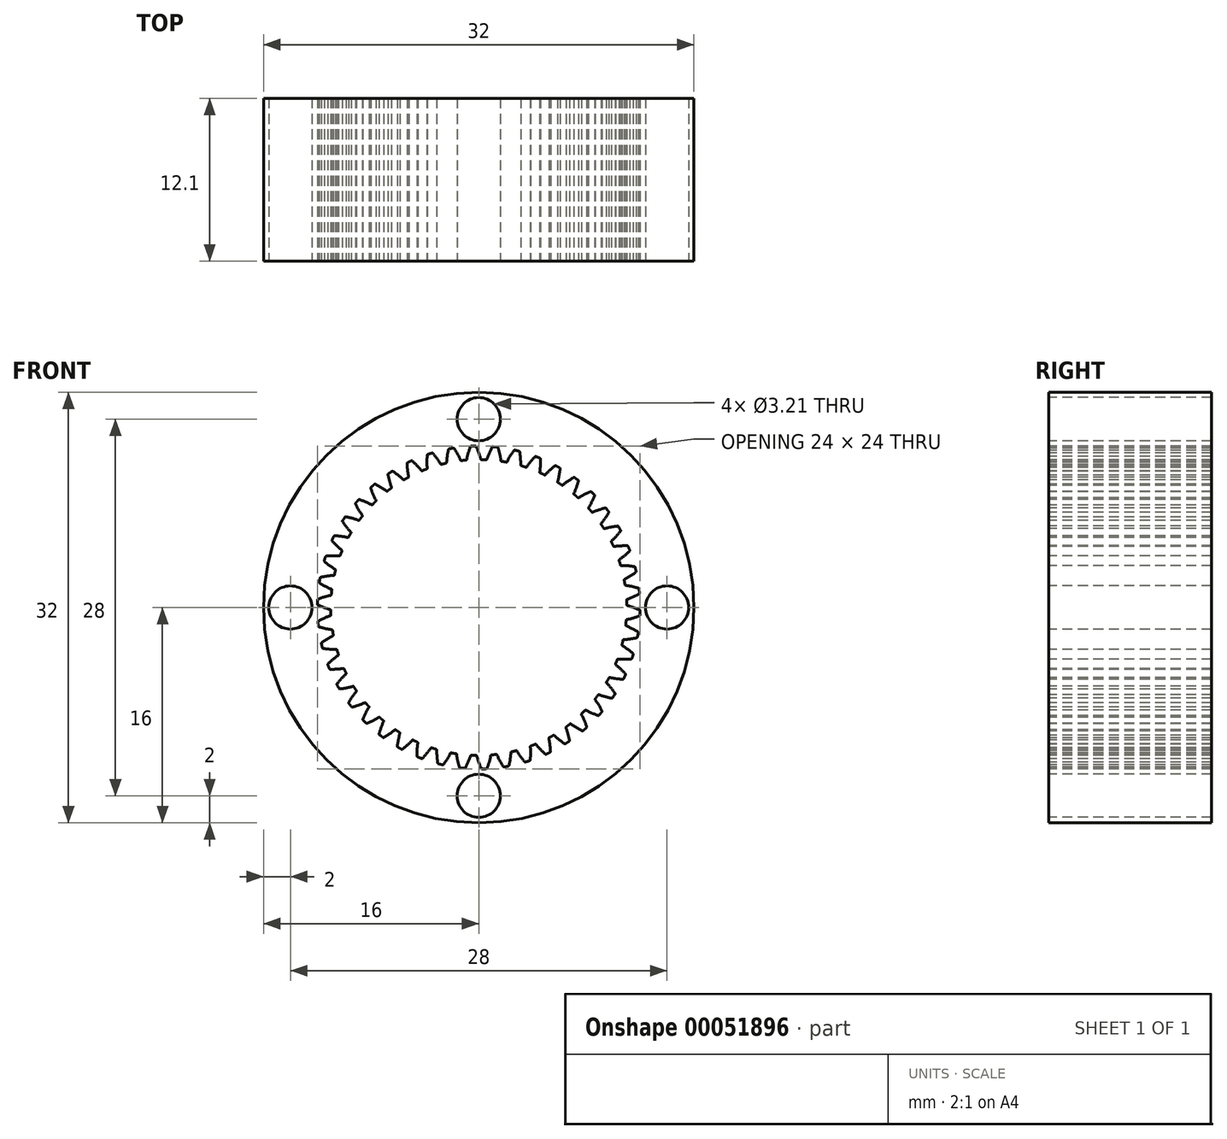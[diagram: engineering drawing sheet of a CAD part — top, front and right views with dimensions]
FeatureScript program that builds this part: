
annotation { "Feature Type Name" : "Feature", "Feature Type Description" : "" }
export const myFeature = defineFeature(function(context is Context, id is Id, definition is map)
    precondition{}
    {
        {
            var Q0;
            Q0=qCreatedBy(makeId("Front.planeOp"),FACE);
            var sketch = newSketch(context, id + "F0", { "sketchPlane" : qUnion([Q0])});
            skCircle(sketch, "E0", {"center": v(0, 0) * mm, "radius": 16 * mm});
            skSolve(sketch);
        }
        {
            var Q0;
            Q0=qSketchRegion(id+"F0",true);
            var Q1;
            Q1=makeQuery(id+"F0.imprint","IMPRINT",FACE,{"disambiguationData":[TD([[makeQuery(id+"F0.imprint","IMPRINT",EDGE,{"derivedFrom":sQuery(id+"F0.wireOp",EDGE,"E0")}),1.0]])]});
            extrude(context, id + "F1", {"entities" : qUnion([Q0, Q1]), "depth" : 12.1 * mm});
        }
        {
            var Q0;
            Q0=makeQuery(id+"F1.opExtrude","CAP_FACE",FACE,{"disambiguationData":[OSD([sQuery(id+"F0.wireOp",EDGE,"E0"),sQuery(id+"F0.wireOp",EDGE,"2902f3af-6cdb-4536-80c8-8346aa25ecb7")])],"isStart":false});
            var sketch = newSketch(context, id + "F2", { "sketchPlane" : qUnion([Q0])});
            skLineSegment(sketch, "E1", {"start": v(0, 27.51) * mm, "end": v(0, -34.9) * mm, "construction": true});
            skCircle(sketch, "E2", {"center": v(0, 14) * mm, "radius": 1.6 * mm});
            skCircle(sketch, "E3.1.0", {"center": v(-14, 0) * mm, "radius": 1.6 * mm});
            skCircle(sketch, "E3.2.0", {"center": v(0, -14) * mm, "radius": 1.6 * mm});
            skCircle(sketch, "E3.3.0", {"center": v(14, 0) * mm, "radius": 1.6 * mm});
            skPoint(sketch, "E3.center", {"position": v(0, 0) * mm});
            skSolve(sketch);
        }
        {
            var Q0;
            Q0=qSketchRegion(id+"F2",true);
            extrude(context, id + "F3", {"entities" : qUnion([Q0]), "operationType" : NewBodyOperationType.REMOVE, "endBound" : BoundingType.THROUGH_ALL, "oppositeDirection" : true, "depth" : 25 * mm});
        }
        {
            var Q0;
            Q0=makeQuery(id+"F1.opExtrude","CAP_FACE",FACE,{"disambiguationData":[OSD([sQuery(id+"F0.wireOp",EDGE,"E0")])],"isStart":false});
            var sketch = newSketch(context, id + "F4", { "sketchPlane" : qUnion([Q0])});
            skCircle(sketch, "E4", {"center": v(0, 0) * mm, "radius": 12 * mm, "construction": true});
            skCircle(sketch, "E5", {"center": v(0, 0) * mm, "radius": 11.5 * mm, "construction": true});
            skCircle(sketch, "E6", {"center": v(0, 0) * mm, "radius": 11 * mm, "construction": true});
            skLineSegment(sketch, "E7", {"start": v(0, 0) * mm, "end": v(0, 20.22) * mm, "construction": true});
            skLineSegment(sketch, "E8", {"start": v(0, 0) * mm, "end": v(-0.7, 20.22) * mm, "construction": true});
            skLineSegment(sketch, "E9", {"start": v(0, 11.5) * mm, "end": v(-8.2, 11.5) * mm, "construction": true});
            skLineSegment(sketch, "E10", {"start": v(0, 11.5) * mm, "end": v(-7.4, 8.8) * mm, "construction": true});
            skCircle(sketch, "E11", {"center": v(0, 11.5) * mm, "radius": 5.75 * mm, "construction": true});
            skCircle(sketch, "E12", {"center": v(-5.4, 9.53) * mm, "radius": 5.75 * mm, "construction": true});
            skArc(sketch, "E13", {"start": v(-0.2, 12) * mm, "mid": v(0, 11.5) * mm, "end": v(0.16, 11) * mm, "construction": true});
            skArc(sketch, "E14.MirrorCS", {"start": v(-0.61, 11.98) * mm, "mid": v(-0.78, 11.48) * mm, "end": v(-0.9, 10.96) * mm, "construction": true});
            skArc(sketch, "E15", {"start": v(-0.62, 11.95) * mm, "mid": v(-0.78, 11.48) * mm, "end": v(-0.9, 11) * mm});
            skArc(sketch, "E16", {"start": v(-0.58, 11.99) * mm, "mid": v(-0.4, 12) * mm, "end": v(-0.24, 12) * mm});
            skArc(sketch, "E17", {"start": v(-0.2, 11.97) * mm, "mid": v(0, 11.5) * mm, "end": v(0.15, 11.04) * mm});
            skArc(sketch, "E18", {"start": v(-0.94, 10.96) * mm, "mid": v(0.38, -11) * mm, "end": v(0.2, 11) * mm});
            skPoint(sketch, "E19.visualSharp", {"position": v(-0.9, 10.96) * mm});
            skArc(sketch, "E19.filletArc", {"start": v(-0.94, 10.96) * mm, "mid": v(-0.92, 10.97) * mm, "end": v(-0.9, 11) * mm});
            skPoint(sketch, "E20.visualSharp", {"position": v(-0.61, 11.98) * mm});
            skArc(sketch, "E20.filletArc", {"start": v(-0.58, 11.99) * mm, "mid": v(-0.6, 11.98) * mm, "end": v(-0.62, 11.95) * mm});
            skPoint(sketch, "E21.visualSharp", {"position": v(-0.2, 12) * mm});
            skArc(sketch, "E21.filletArc", {"start": v(-0.2, 11.97) * mm, "mid": v(-0.21, 12) * mm, "end": v(-0.24, 12) * mm});
            skPoint(sketch, "E22.visualSharp", {"position": v(0.16, 11) * mm});
            skArc(sketch, "E22.filletArc", {"start": v(0.15, 11.04) * mm, "mid": v(0.16, 11) * mm, "end": v(0.2, 11) * mm});
            skArc(sketch, "E23.1.0", {"start": v(-2.43, 10.73) * mm, "mid": v(-2.4, 10.75) * mm, "end": v(-2.39, 10.77) * mm});
            skArc(sketch, "E23.1.1", {"start": v(-2.24, 11.76) * mm, "mid": v(-2.34, 11.27) * mm, "end": v(-2.39, 10.77) * mm});
            skArc(sketch, "E23.1.2", {"start": v(-2.2, 11.8) * mm, "mid": v(-2.23, 11.78) * mm, "end": v(-2.24, 11.76) * mm});
            skArc(sketch, "E23.1.3", {"start": v(-2.2, 11.8) * mm, "mid": v(-2.04, 11.83) * mm, "end": v(-1.87, 11.85) * mm});
            skArc(sketch, "E23.1.4", {"start": v(-1.82, 11.83) * mm, "mid": v(-1.84, 11.85) * mm, "end": v(-1.87, 11.85) * mm});
            skArc(sketch, "E23.1.5", {"start": v(-1.82, 11.83) * mm, "mid": v(-1.57, 11.4) * mm, "end": v(-1.36, 10.95) * mm});
            skArc(sketch, "E23.1.6", {"start": v(-1.36, 10.95) * mm, "mid": v(-1.34, 10.93) * mm, "end": v(-1.3, 10.92) * mm});
            skArc(sketch, "E23.2.0", {"start": v(-3.87, 10.3) * mm, "mid": v(-3.84, 10.32) * mm, "end": v(-3.83, 10.35) * mm});
            skArc(sketch, "E23.2.1", {"start": v(-3.82, 11.34) * mm, "mid": v(-3.85, 10.85) * mm, "end": v(-3.83, 10.35) * mm});
            skArc(sketch, "E23.2.2", {"start": v(-3.8, 11.39) * mm, "mid": v(-3.81, 11.37) * mm, "end": v(-3.82, 11.34) * mm});
            skArc(sketch, "E23.2.3", {"start": v(-3.8, 11.39) * mm, "mid": v(-3.63, 11.44) * mm, "end": v(-3.47, 11.49) * mm});
            skArc(sketch, "E23.2.4", {"start": v(-3.42, 11.47) * mm, "mid": v(-3.44, 11.49) * mm, "end": v(-3.47, 11.49) * mm});
            skArc(sketch, "E23.2.5", {"start": v(-3.42, 11.47) * mm, "mid": v(-3.1, 11.08) * mm, "end": v(-2.84, 10.67) * mm});
            skArc(sketch, "E23.2.6", {"start": v(-2.84, 10.67) * mm, "mid": v(-2.81, 10.65) * mm, "end": v(-2.78, 10.64) * mm});
            skArc(sketch, "E23.3.0", {"start": v(-5.23, 9.68) * mm, "mid": v(-5.21, 9.7) * mm, "end": v(-5.2, 9.73) * mm});
            skArc(sketch, "E23.3.1", {"start": v(-5.33, 10.72) * mm, "mid": v(-5.3, 10.22) * mm, "end": v(-5.2, 9.73) * mm});
            skArc(sketch, "E23.3.2", {"start": v(-5.3, 10.76) * mm, "mid": v(-5.33, 10.74) * mm, "end": v(-5.33, 10.72) * mm});
            skArc(sketch, "E23.3.3", {"start": v(-5.3, 10.76) * mm, "mid": v(-5.15, 10.84) * mm, "end": v(-5, 10.9) * mm});
            skArc(sketch, "E23.3.4", {"start": v(-4.95, 10.9) * mm, "mid": v(-4.97, 10.91) * mm, "end": v(-5, 10.9) * mm});
            skArc(sketch, "E23.3.5", {"start": v(-4.95, 10.9) * mm, "mid": v(-4.59, 10.56) * mm, "end": v(-4.26, 10.18) * mm});
            skArc(sketch, "E23.3.6", {"start": v(-4.26, 10.18) * mm, "mid": v(-4.23, 10.16) * mm, "end": v(-4.2, 10.17) * mm});
            skArc(sketch, "E23.4.0", {"start": v(-6.5, 8.87) * mm, "mid": v(-6.48, 8.9) * mm, "end": v(-6.48, 8.93) * mm});
            skArc(sketch, "E23.4.1", {"start": v(-6.74, 9.9) * mm, "mid": v(-6.63, 9.4) * mm, "end": v(-6.48, 8.93) * mm});
            skArc(sketch, "E23.4.2", {"start": v(-6.72, 9.94) * mm, "mid": v(-6.74, 9.92) * mm, "end": v(-6.74, 9.9) * mm});
            skArc(sketch, "E23.4.3", {"start": v(-6.72, 9.94) * mm, "mid": v(-6.58, 10.03) * mm, "end": v(-6.44, 10.13) * mm});
            skArc(sketch, "E23.4.4", {"start": v(-6.38, 10.13) * mm, "mid": v(-6.41, 10.13) * mm, "end": v(-6.44, 10.13) * mm});
            skArc(sketch, "E23.4.5", {"start": v(-6.38, 10.13) * mm, "mid": v(-5.98, 9.83) * mm, "end": v(-5.6, 9.5) * mm});
            skArc(sketch, "E23.4.6", {"start": v(-5.6, 9.5) * mm, "mid": v(-5.58, 9.5) * mm, "end": v(-5.55, 9.5) * mm});
            skArc(sketch, "E23.5.0", {"start": v(-7.65, 7.9) * mm, "mid": v(-7.63, 7.93) * mm, "end": v(-7.64, 7.96) * mm});
            skArc(sketch, "E23.5.1", {"start": v(-8.03, 8.88) * mm, "mid": v(-7.85, 8.41) * mm, "end": v(-7.64, 7.96) * mm});
            skArc(sketch, "E23.5.2", {"start": v(-8.01, 8.93) * mm, "mid": v(-8.03, 8.9) * mm, "end": v(-8.03, 8.88) * mm});
            skArc(sketch, "E23.5.3", {"start": v(-8.01, 8.93) * mm, "mid": v(-7.89, 9.04) * mm, "end": v(-7.76, 9.15) * mm});
            skArc(sketch, "E23.5.4", {"start": v(-7.7, 9.16) * mm, "mid": v(-7.73, 9.17) * mm, "end": v(-7.76, 9.15) * mm});
            skArc(sketch, "E23.5.5", {"start": v(-7.7, 9.16) * mm, "mid": v(-7.27, 8.93) * mm, "end": v(-6.85, 8.65) * mm});
            skArc(sketch, "E23.5.6", {"start": v(-6.85, 8.65) * mm, "mid": v(-6.82, 8.64) * mm, "end": v(-6.79, 8.65) * mm});
            skArc(sketch, "E23.6.0", {"start": v(-8.65, 6.79) * mm, "mid": v(-8.64, 6.82) * mm, "end": v(-8.65, 6.85) * mm});
            skArc(sketch, "E23.6.1", {"start": v(-9.16, 7.7) * mm, "mid": v(-8.93, 7.27) * mm, "end": v(-8.65, 6.85) * mm});
            skArc(sketch, "E23.6.2", {"start": v(-9.15, 7.76) * mm, "mid": v(-9.17, 7.73) * mm, "end": v(-9.16, 7.7) * mm});
            skArc(sketch, "E23.6.3", {"start": v(-9.15, 7.76) * mm, "mid": v(-9.04, 7.89) * mm, "end": v(-8.93, 8.01) * mm});
            skArc(sketch, "E23.6.4", {"start": v(-8.88, 8.03) * mm, "mid": v(-8.9, 8.03) * mm, "end": v(-8.93, 8.01) * mm});
            skArc(sketch, "E23.6.5", {"start": v(-8.88, 8.03) * mm, "mid": v(-8.41, 7.85) * mm, "end": v(-7.96, 7.64) * mm});
            skArc(sketch, "E23.6.6", {"start": v(-7.96, 7.64) * mm, "mid": v(-7.93, 7.63) * mm, "end": v(-7.9, 7.65) * mm});
            skArc(sketch, "E23.7.0", {"start": v(-9.5, 5.55) * mm, "mid": v(-9.5, 5.58) * mm, "end": v(-9.5, 5.6) * mm});
            skArc(sketch, "E23.7.1", {"start": v(-10.13, 6.38) * mm, "mid": v(-9.83, 5.98) * mm, "end": v(-9.5, 5.6) * mm});
            skArc(sketch, "E23.7.2", {"start": v(-10.13, 6.44) * mm, "mid": v(-10.13, 6.41) * mm, "end": v(-10.13, 6.38) * mm});
            skArc(sketch, "E23.7.3", {"start": v(-10.13, 6.44) * mm, "mid": v(-10.03, 6.58) * mm, "end": v(-9.94, 6.72) * mm});
            skArc(sketch, "E23.7.4", {"start": v(-9.9, 6.74) * mm, "mid": v(-9.92, 6.74) * mm, "end": v(-9.94, 6.72) * mm});
            skArc(sketch, "E23.7.5", {"start": v(-9.9, 6.74) * mm, "mid": v(-9.4, 6.63) * mm, "end": v(-8.93, 6.48) * mm});
            skArc(sketch, "E23.7.6", {"start": v(-8.93, 6.48) * mm, "mid": v(-8.9, 6.48) * mm, "end": v(-8.87, 6.5) * mm});
            skArc(sketch, "E23.8.0", {"start": v(-10.17, 4.2) * mm, "mid": v(-10.16, 4.23) * mm, "end": v(-10.18, 4.26) * mm});
            skArc(sketch, "E23.8.1", {"start": v(-10.9, 4.95) * mm, "mid": v(-10.56, 4.59) * mm, "end": v(-10.18, 4.26) * mm});
            skArc(sketch, "E23.8.2", {"start": v(-10.9, 5) * mm, "mid": v(-10.91, 4.97) * mm, "end": v(-10.9, 4.95) * mm});
            skArc(sketch, "E23.8.3", {"start": v(-10.9, 5) * mm, "mid": v(-10.84, 5.15) * mm, "end": v(-10.76, 5.3) * mm});
            skArc(sketch, "E23.8.4", {"start": v(-10.72, 5.33) * mm, "mid": v(-10.74, 5.33) * mm, "end": v(-10.76, 5.3) * mm});
            skArc(sketch, "E23.8.5", {"start": v(-10.72, 5.33) * mm, "mid": v(-10.22, 5.3) * mm, "end": v(-9.73, 5.2) * mm});
            skArc(sketch, "E23.8.6", {"start": v(-9.73, 5.2) * mm, "mid": v(-9.7, 5.21) * mm, "end": v(-9.68, 5.23) * mm});
            skArc(sketch, "E23.9.0", {"start": v(-10.64, 2.78) * mm, "mid": v(-10.65, 2.81) * mm, "end": v(-10.67, 2.84) * mm});
            skArc(sketch, "E23.9.1", {"start": v(-11.47, 3.42) * mm, "mid": v(-11.08, 3.1) * mm, "end": v(-10.67, 2.84) * mm});
            skArc(sketch, "E23.9.2", {"start": v(-11.49, 3.47) * mm, "mid": v(-11.49, 3.44) * mm, "end": v(-11.47, 3.42) * mm});
            skArc(sketch, "E23.9.3", {"start": v(-11.49, 3.47) * mm, "mid": v(-11.44, 3.63) * mm, "end": v(-11.39, 3.8) * mm});
            skArc(sketch, "E23.9.4", {"start": v(-11.34, 3.82) * mm, "mid": v(-11.37, 3.81) * mm, "end": v(-11.39, 3.8) * mm});
            skArc(sketch, "E23.9.5", {"start": v(-11.34, 3.82) * mm, "mid": v(-10.85, 3.85) * mm, "end": v(-10.35, 3.83) * mm});
            skArc(sketch, "E23.9.6", {"start": v(-10.35, 3.83) * mm, "mid": v(-10.32, 3.84) * mm, "end": v(-10.3, 3.87) * mm});
            skArc(sketch, "E23.10.0", {"start": v(-10.92, 1.3) * mm, "mid": v(-10.93, 1.34) * mm, "end": v(-10.95, 1.36) * mm});
            skArc(sketch, "E23.10.1", {"start": v(-11.83, 1.82) * mm, "mid": v(-11.4, 1.57) * mm, "end": v(-10.95, 1.36) * mm});
            skArc(sketch, "E23.10.2", {"start": v(-11.85, 1.87) * mm, "mid": v(-11.85, 1.84) * mm, "end": v(-11.83, 1.82) * mm});
            skArc(sketch, "E23.10.3", {"start": v(-11.85, 1.87) * mm, "mid": v(-11.83, 2.04) * mm, "end": v(-11.8, 2.2) * mm});
            skArc(sketch, "E23.10.4", {"start": v(-11.76, 2.24) * mm, "mid": v(-11.78, 2.23) * mm, "end": v(-11.8, 2.2) * mm});
            skArc(sketch, "E23.10.5", {"start": v(-11.76, 2.24) * mm, "mid": v(-11.27, 2.34) * mm, "end": v(-10.77, 2.39) * mm});
            skArc(sketch, "E23.10.6", {"start": v(-10.77, 2.39) * mm, "mid": v(-10.75, 2.4) * mm, "end": v(-10.73, 2.43) * mm});
            skArc(sketch, "E23.11.0", {"start": v(-11, -0.2) * mm, "mid": v(-11, -0.16) * mm, "end": v(-11.04, -0.15) * mm});
            skArc(sketch, "E23.11.1", {"start": v(-11.97, 0.2) * mm, "mid": v(-11.5, 0) * mm, "end": v(-11.04, -0.15) * mm});
            skArc(sketch, "E23.11.2", {"start": v(-12, 0.24) * mm, "mid": v(-12, 0.21) * mm, "end": v(-11.97, 0.2) * mm});
            skArc(sketch, "E23.11.3", {"start": v(-12, 0.24) * mm, "mid": v(-12, 0.4) * mm, "end": v(-11.99, 0.58) * mm});
            skArc(sketch, "E23.11.4", {"start": v(-11.95, 0.62) * mm, "mid": v(-11.98, 0.6) * mm, "end": v(-11.99, 0.58) * mm});
            skArc(sketch, "E23.11.5", {"start": v(-11.95, 0.62) * mm, "mid": v(-11.48, 0.78) * mm, "end": v(-11, 0.9) * mm});
            skArc(sketch, "E23.11.6", {"start": v(-11, 0.9) * mm, "mid": v(-10.97, 0.92) * mm, "end": v(-10.96, 0.94) * mm});
            skArc(sketch, "E23.12.0", {"start": v(-10.87, -1.7) * mm, "mid": v(-10.88, -1.66) * mm, "end": v(-10.91, -1.65) * mm});
            skArc(sketch, "E23.12.1", {"start": v(-11.88, -1.44) * mm, "mid": v(-11.4, -1.56) * mm, "end": v(-10.91, -1.65) * mm});
            skArc(sketch, "E23.12.2", {"start": v(-11.92, -1.4) * mm, "mid": v(-11.9, -1.42) * mm, "end": v(-11.88, -1.44) * mm});
            skArc(sketch, "E23.12.3", {"start": v(-11.92, -1.4) * mm, "mid": v(-11.94, -1.23) * mm, "end": v(-11.95, -1.06) * mm});
            skArc(sketch, "E23.12.4", {"start": v(-11.93, -1.01) * mm, "mid": v(-11.95, -1.03) * mm, "end": v(-11.95, -1.06) * mm});
            skArc(sketch, "E23.12.5", {"start": v(-11.93, -1.01) * mm, "mid": v(-11.48, -0.79) * mm, "end": v(-11.02, -0.6) * mm});
            skArc(sketch, "E23.12.6", {"start": v(-11.02, -0.6) * mm, "mid": v(-11, -0.59) * mm, "end": v(-10.99, -0.56) * mm});
            skArc(sketch, "E23.13.0", {"start": v(-10.54, -3.15) * mm, "mid": v(-10.56, -3.13) * mm, "end": v(-10.59, -3.12) * mm});
            skArc(sketch, "E23.13.1", {"start": v(-11.58, -3.04) * mm, "mid": v(-11.08, -3.1) * mm, "end": v(-10.59, -3.12) * mm});
            skArc(sketch, "E23.13.2", {"start": v(-11.62, -3) * mm, "mid": v(-11.6, -3.03) * mm, "end": v(-11.58, -3.04) * mm});
            skArc(sketch, "E23.13.3", {"start": v(-11.62, -3) * mm, "mid": v(-11.66, -2.84) * mm, "end": v(-11.7, -2.68) * mm});
            skArc(sketch, "E23.13.4", {"start": v(-11.68, -2.63) * mm, "mid": v(-11.7, -2.65) * mm, "end": v(-11.7, -2.68) * mm});
            skArc(sketch, "E23.13.5", {"start": v(-11.68, -2.63) * mm, "mid": v(-11.27, -2.35) * mm, "end": v(-10.83, -2.1) * mm});
            skArc(sketch, "E23.13.6", {"start": v(-10.83, -2.1) * mm, "mid": v(-10.81, -2.08) * mm, "end": v(-10.8, -2.05) * mm});
            skArc(sketch, "E23.14.0", {"start": v(-10.01, -4.56) * mm, "mid": v(-10.03, -4.54) * mm, "end": v(-10.06, -4.53) * mm});
            skArc(sketch, "E23.14.1", {"start": v(-11.06, -4.6) * mm, "mid": v(-10.56, -4.58) * mm, "end": v(-10.06, -4.53) * mm});
            skArc(sketch, "E23.14.2", {"start": v(-11.1, -4.56) * mm, "mid": v(-11.08, -4.58) * mm, "end": v(-11.06, -4.6) * mm});
            skArc(sketch, "E23.14.3", {"start": v(-11.1, -4.56) * mm, "mid": v(-11.16, -4.4) * mm, "end": v(-11.22, -4.24) * mm});
            skArc(sketch, "E23.14.4", {"start": v(-11.21, -4.2) * mm, "mid": v(-11.23, -4.22) * mm, "end": v(-11.22, -4.24) * mm});
            skArc(sketch, "E23.14.5", {"start": v(-11.21, -4.2) * mm, "mid": v(-10.84, -3.86) * mm, "end": v(-10.45, -3.56) * mm});
            skArc(sketch, "E23.14.6", {"start": v(-10.45, -3.56) * mm, "mid": v(-10.43, -3.53) * mm, "end": v(-10.43, -3.5) * mm});
            skArc(sketch, "E23.15.0", {"start": v(-9.3, -5.88) * mm, "mid": v(-9.32, -5.86) * mm, "end": v(-9.35, -5.86) * mm});
            skArc(sketch, "E23.15.1", {"start": v(-10.33, -6.05) * mm, "mid": v(-9.84, -5.98) * mm, "end": v(-9.35, -5.86) * mm});
            skArc(sketch, "E23.15.2", {"start": v(-10.38, -6.03) * mm, "mid": v(-10.36, -6.05) * mm, "end": v(-10.33, -6.05) * mm});
            skArc(sketch, "E23.15.3", {"start": v(-10.38, -6.03) * mm, "mid": v(-10.46, -5.88) * mm, "end": v(-10.54, -5.73) * mm});
            skArc(sketch, "E23.15.4", {"start": v(-10.54, -5.68) * mm, "mid": v(-10.55, -5.7) * mm, "end": v(-10.54, -5.73) * mm});
            skArc(sketch, "E23.15.5", {"start": v(-10.54, -5.68) * mm, "mid": v(-10.22, -5.3) * mm, "end": v(-9.87, -4.95) * mm});
            skArc(sketch, "E23.15.6", {"start": v(-9.87, -4.95) * mm, "mid": v(-9.85, -4.92) * mm, "end": v(-9.85, -4.89) * mm});
            skArc(sketch, "E23.16.0", {"start": v(-8.4, -7.1) * mm, "mid": v(-8.44, -7.08) * mm, "end": v(-8.47, -7.08) * mm});
            skArc(sketch, "E23.16.1", {"start": v(-9.4, -7.4) * mm, "mid": v(-8.93, -7.26) * mm, "end": v(-8.47, -7.08) * mm});
            skArc(sketch, "E23.16.2", {"start": v(-9.46, -7.38) * mm, "mid": v(-9.44, -7.4) * mm, "end": v(-9.4, -7.4) * mm});
            skArc(sketch, "E23.16.3", {"start": v(-9.46, -7.38) * mm, "mid": v(-9.56, -7.25) * mm, "end": v(-9.66, -7.12) * mm});
            skArc(sketch, "E23.16.4", {"start": v(-9.67, -7.06) * mm, "mid": v(-9.67, -7.09) * mm, "end": v(-9.66, -7.12) * mm});
            skArc(sketch, "E23.16.5", {"start": v(-9.67, -7.06) * mm, "mid": v(-9.4, -6.64) * mm, "end": v(-9.1, -6.24) * mm});
            skArc(sketch, "E23.16.6", {"start": v(-9.1, -6.24) * mm, "mid": v(-9.09, -6.21) * mm, "end": v(-9.1, -6.18) * mm});
            skArc(sketch, "E23.17.0", {"start": v(-7.36, -8.17) * mm, "mid": v(-7.4, -8.16) * mm, "end": v(-7.42, -8.17) * mm});
            skArc(sketch, "E23.17.1", {"start": v(-8.31, -8.61) * mm, "mid": v(-7.86, -8.4) * mm, "end": v(-7.42, -8.17) * mm});
            skArc(sketch, "E23.17.2", {"start": v(-8.36, -8.6) * mm, "mid": v(-8.34, -8.62) * mm, "end": v(-8.31, -8.61) * mm});
            skArc(sketch, "E23.17.3", {"start": v(-8.36, -8.6) * mm, "mid": v(-8.49, -8.49) * mm, "end": v(-8.6, -8.36) * mm});
            skArc(sketch, "E23.17.4", {"start": v(-8.61, -8.31) * mm, "mid": v(-8.62, -8.34) * mm, "end": v(-8.6, -8.36) * mm});
            skArc(sketch, "E23.17.5", {"start": v(-8.61, -8.31) * mm, "mid": v(-8.4, -7.86) * mm, "end": v(-8.17, -7.42) * mm});
            skArc(sketch, "E23.17.6", {"start": v(-8.17, -7.42) * mm, "mid": v(-8.16, -7.4) * mm, "end": v(-8.17, -7.36) * mm});
            skArc(sketch, "E23.18.0", {"start": v(-6.18, -9.1) * mm, "mid": v(-6.21, -9.09) * mm, "end": v(-6.24, -9.1) * mm});
            skArc(sketch, "E23.18.1", {"start": v(-7.06, -9.67) * mm, "mid": v(-6.64, -9.4) * mm, "end": v(-6.24, -9.1) * mm});
            skArc(sketch, "E23.18.2", {"start": v(-7.12, -9.66) * mm, "mid": v(-7.09, -9.67) * mm, "end": v(-7.06, -9.67) * mm});
            skArc(sketch, "E23.18.3", {"start": v(-7.12, -9.66) * mm, "mid": v(-7.25, -9.56) * mm, "end": v(-7.38, -9.46) * mm});
            skArc(sketch, "E23.18.4", {"start": v(-7.4, -9.4) * mm, "mid": v(-7.4, -9.44) * mm, "end": v(-7.38, -9.46) * mm});
            skArc(sketch, "E23.18.5", {"start": v(-7.4, -9.4) * mm, "mid": v(-7.26, -8.93) * mm, "end": v(-7.08, -8.47) * mm});
            skArc(sketch, "E23.18.6", {"start": v(-7.08, -8.47) * mm, "mid": v(-7.08, -8.44) * mm, "end": v(-7.1, -8.4) * mm});
            skArc(sketch, "E23.19.0", {"start": v(-4.89, -9.85) * mm, "mid": v(-4.92, -9.85) * mm, "end": v(-4.95, -9.87) * mm});
            skArc(sketch, "E23.19.1", {"start": v(-5.68, -10.54) * mm, "mid": v(-5.3, -10.22) * mm, "end": v(-4.95, -9.87) * mm});
            skArc(sketch, "E23.19.2", {"start": v(-5.73, -10.54) * mm, "mid": v(-5.7, -10.55) * mm, "end": v(-5.68, -10.54) * mm});
            skArc(sketch, "E23.19.3", {"start": v(-5.73, -10.54) * mm, "mid": v(-5.88, -10.46) * mm, "end": v(-6.03, -10.38) * mm});
            skArc(sketch, "E23.19.4", {"start": v(-6.05, -10.33) * mm, "mid": v(-6.05, -10.36) * mm, "end": v(-6.03, -10.38) * mm});
            skArc(sketch, "E23.19.5", {"start": v(-6.05, -10.33) * mm, "mid": v(-5.98, -9.84) * mm, "end": v(-5.86, -9.35) * mm});
            skArc(sketch, "E23.19.6", {"start": v(-5.86, -9.35) * mm, "mid": v(-5.86, -9.32) * mm, "end": v(-5.88, -9.3) * mm});
            skArc(sketch, "E23.20.0", {"start": v(-3.5, -10.43) * mm, "mid": v(-3.53, -10.43) * mm, "end": v(-3.56, -10.45) * mm});
            skArc(sketch, "E23.20.1", {"start": v(-4.2, -11.21) * mm, "mid": v(-3.86, -10.84) * mm, "end": v(-3.56, -10.45) * mm});
            skArc(sketch, "E23.20.2", {"start": v(-4.24, -11.22) * mm, "mid": v(-4.22, -11.23) * mm, "end": v(-4.2, -11.21) * mm});
            skArc(sketch, "E23.20.3", {"start": v(-4.24, -11.22) * mm, "mid": v(-4.4, -11.16) * mm, "end": v(-4.56, -11.1) * mm});
            skArc(sketch, "E23.20.4", {"start": v(-4.6, -11.06) * mm, "mid": v(-4.58, -11.08) * mm, "end": v(-4.56, -11.1) * mm});
            skArc(sketch, "E23.20.5", {"start": v(-4.6, -11.06) * mm, "mid": v(-4.58, -10.56) * mm, "end": v(-4.53, -10.06) * mm});
            skArc(sketch, "E23.20.6", {"start": v(-4.53, -10.06) * mm, "mid": v(-4.54, -10.03) * mm, "end": v(-4.56, -10.01) * mm});
            skArc(sketch, "E23.21.0", {"start": v(-2.05, -10.8) * mm, "mid": v(-2.08, -10.81) * mm, "end": v(-2.1, -10.83) * mm});
            skArc(sketch, "E23.21.1", {"start": v(-2.63, -11.68) * mm, "mid": v(-2.35, -11.27) * mm, "end": v(-2.1, -10.83) * mm});
            skArc(sketch, "E23.21.2", {"start": v(-2.68, -11.7) * mm, "mid": v(-2.65, -11.7) * mm, "end": v(-2.63, -11.68) * mm});
            skArc(sketch, "E23.21.3", {"start": v(-2.68, -11.7) * mm, "mid": v(-2.84, -11.66) * mm, "end": v(-3, -11.62) * mm});
            skArc(sketch, "E23.21.4", {"start": v(-3.04, -11.58) * mm, "mid": v(-3.03, -11.6) * mm, "end": v(-3, -11.62) * mm});
            skArc(sketch, "E23.21.5", {"start": v(-3.04, -11.58) * mm, "mid": v(-3.1, -11.08) * mm, "end": v(-3.12, -10.59) * mm});
            skArc(sketch, "E23.21.6", {"start": v(-3.12, -10.59) * mm, "mid": v(-3.13, -10.56) * mm, "end": v(-3.15, -10.54) * mm});
            skArc(sketch, "E23.22.0", {"start": v(-0.56, -10.99) * mm, "mid": v(-0.59, -11) * mm, "end": v(-0.6, -11.02) * mm});
            skArc(sketch, "E23.22.1", {"start": v(-1.01, -11.93) * mm, "mid": v(-0.79, -11.48) * mm, "end": v(-0.6, -11.02) * mm});
            skArc(sketch, "E23.22.2", {"start": v(-1.06, -11.95) * mm, "mid": v(-1.03, -11.95) * mm, "end": v(-1.01, -11.93) * mm});
            skArc(sketch, "E23.22.3", {"start": v(-1.06, -11.95) * mm, "mid": v(-1.23, -11.94) * mm, "end": v(-1.4, -11.92) * mm});
            skArc(sketch, "E23.22.4", {"start": v(-1.44, -11.88) * mm, "mid": v(-1.42, -11.9) * mm, "end": v(-1.4, -11.92) * mm});
            skArc(sketch, "E23.22.5", {"start": v(-1.44, -11.88) * mm, "mid": v(-1.56, -11.4) * mm, "end": v(-1.65, -10.91) * mm});
            skArc(sketch, "E23.22.6", {"start": v(-1.65, -10.91) * mm, "mid": v(-1.66, -10.88) * mm, "end": v(-1.7, -10.87) * mm});
            skArc(sketch, "E23.23.0", {"start": v(0.94, -10.96) * mm, "mid": v(0.92, -10.97) * mm, "end": v(0.9, -11) * mm});
            skArc(sketch, "E23.23.1", {"start": v(0.62, -11.95) * mm, "mid": v(0.78, -11.48) * mm, "end": v(0.9, -11) * mm});
            skArc(sketch, "E23.23.2", {"start": v(0.58, -11.99) * mm, "mid": v(0.6, -11.98) * mm, "end": v(0.62, -11.95) * mm});
            skArc(sketch, "E23.23.3", {"start": v(0.58, -11.99) * mm, "mid": v(0.4, -12) * mm, "end": v(0.24, -12) * mm});
            skArc(sketch, "E23.23.4", {"start": v(0.2, -11.97) * mm, "mid": v(0.21, -12) * mm, "end": v(0.24, -12) * mm});
            skArc(sketch, "E23.23.5", {"start": v(0.2, -11.97) * mm, "mid": v(0, -11.5) * mm, "end": v(-0.15, -11.04) * mm});
            skArc(sketch, "E23.23.6", {"start": v(-0.15, -11.04) * mm, "mid": v(-0.16, -11) * mm, "end": v(-0.2, -11) * mm});
            skArc(sketch, "E23.24.0", {"start": v(2.43, -10.73) * mm, "mid": v(2.4, -10.75) * mm, "end": v(2.39, -10.77) * mm});
            skArc(sketch, "E23.24.1", {"start": v(2.24, -11.76) * mm, "mid": v(2.34, -11.27) * mm, "end": v(2.39, -10.77) * mm});
            skArc(sketch, "E23.24.2", {"start": v(2.2, -11.8) * mm, "mid": v(2.23, -11.78) * mm, "end": v(2.24, -11.76) * mm});
            skArc(sketch, "E23.24.3", {"start": v(2.2, -11.8) * mm, "mid": v(2.04, -11.83) * mm, "end": v(1.87, -11.85) * mm});
            skArc(sketch, "E23.24.4", {"start": v(1.82, -11.83) * mm, "mid": v(1.84, -11.85) * mm, "end": v(1.87, -11.85) * mm});
            skArc(sketch, "E23.24.5", {"start": v(1.82, -11.83) * mm, "mid": v(1.57, -11.4) * mm, "end": v(1.36, -10.95) * mm});
            skArc(sketch, "E23.24.6", {"start": v(1.36, -10.95) * mm, "mid": v(1.34, -10.93) * mm, "end": v(1.3, -10.92) * mm});
            skArc(sketch, "E23.25.0", {"start": v(3.87, -10.3) * mm, "mid": v(3.84, -10.32) * mm, "end": v(3.83, -10.35) * mm});
            skArc(sketch, "E23.25.1", {"start": v(3.82, -11.34) * mm, "mid": v(3.85, -10.85) * mm, "end": v(3.83, -10.35) * mm});
            skArc(sketch, "E23.25.2", {"start": v(3.8, -11.39) * mm, "mid": v(3.81, -11.37) * mm, "end": v(3.82, -11.34) * mm});
            skArc(sketch, "E23.25.3", {"start": v(3.8, -11.39) * mm, "mid": v(3.63, -11.44) * mm, "end": v(3.47, -11.49) * mm});
            skArc(sketch, "E23.25.4", {"start": v(3.42, -11.47) * mm, "mid": v(3.44, -11.49) * mm, "end": v(3.47, -11.49) * mm});
            skArc(sketch, "E23.25.5", {"start": v(3.42, -11.47) * mm, "mid": v(3.1, -11.08) * mm, "end": v(2.84, -10.67) * mm});
            skArc(sketch, "E23.25.6", {"start": v(2.84, -10.67) * mm, "mid": v(2.81, -10.65) * mm, "end": v(2.78, -10.64) * mm});
            skArc(sketch, "E23.26.0", {"start": v(5.23, -9.68) * mm, "mid": v(5.21, -9.7) * mm, "end": v(5.2, -9.73) * mm});
            skArc(sketch, "E23.26.1", {"start": v(5.33, -10.72) * mm, "mid": v(5.3, -10.22) * mm, "end": v(5.2, -9.73) * mm});
            skArc(sketch, "E23.26.2", {"start": v(5.3, -10.76) * mm, "mid": v(5.33, -10.74) * mm, "end": v(5.33, -10.72) * mm});
            skArc(sketch, "E23.26.3", {"start": v(5.3, -10.76) * mm, "mid": v(5.15, -10.84) * mm, "end": v(5, -10.9) * mm});
            skArc(sketch, "E23.26.4", {"start": v(4.95, -10.9) * mm, "mid": v(4.97, -10.91) * mm, "end": v(5, -10.9) * mm});
            skArc(sketch, "E23.26.5", {"start": v(4.95, -10.9) * mm, "mid": v(4.59, -10.56) * mm, "end": v(4.26, -10.18) * mm});
            skArc(sketch, "E23.26.6", {"start": v(4.26, -10.18) * mm, "mid": v(4.23, -10.16) * mm, "end": v(4.2, -10.17) * mm});
            skArc(sketch, "E23.27.0", {"start": v(6.5, -8.87) * mm, "mid": v(6.48, -8.9) * mm, "end": v(6.48, -8.93) * mm});
            skArc(sketch, "E23.27.1", {"start": v(6.74, -9.9) * mm, "mid": v(6.63, -9.4) * mm, "end": v(6.48, -8.93) * mm});
            skArc(sketch, "E23.27.2", {"start": v(6.72, -9.94) * mm, "mid": v(6.74, -9.92) * mm, "end": v(6.74, -9.9) * mm});
            skArc(sketch, "E23.27.3", {"start": v(6.72, -9.94) * mm, "mid": v(6.58, -10.03) * mm, "end": v(6.44, -10.13) * mm});
            skArc(sketch, "E23.27.4", {"start": v(6.38, -10.13) * mm, "mid": v(6.41, -10.13) * mm, "end": v(6.44, -10.13) * mm});
            skArc(sketch, "E23.27.5", {"start": v(6.38, -10.13) * mm, "mid": v(5.98, -9.83) * mm, "end": v(5.6, -9.5) * mm});
            skArc(sketch, "E23.27.6", {"start": v(5.6, -9.5) * mm, "mid": v(5.58, -9.5) * mm, "end": v(5.55, -9.5) * mm});
            skArc(sketch, "E23.28.0", {"start": v(7.65, -7.9) * mm, "mid": v(7.63, -7.93) * mm, "end": v(7.64, -7.96) * mm});
            skArc(sketch, "E23.28.1", {"start": v(8.03, -8.88) * mm, "mid": v(7.85, -8.41) * mm, "end": v(7.64, -7.96) * mm});
            skArc(sketch, "E23.28.2", {"start": v(8.01, -8.93) * mm, "mid": v(8.03, -8.9) * mm, "end": v(8.03, -8.88) * mm});
            skArc(sketch, "E23.28.3", {"start": v(8.01, -8.93) * mm, "mid": v(7.89, -9.04) * mm, "end": v(7.76, -9.15) * mm});
            skArc(sketch, "E23.28.4", {"start": v(7.7, -9.16) * mm, "mid": v(7.73, -9.17) * mm, "end": v(7.76, -9.15) * mm});
            skArc(sketch, "E23.28.5", {"start": v(7.7, -9.16) * mm, "mid": v(7.27, -8.93) * mm, "end": v(6.85, -8.65) * mm});
            skArc(sketch, "E23.28.6", {"start": v(6.85, -8.65) * mm, "mid": v(6.82, -8.64) * mm, "end": v(6.79, -8.65) * mm});
            skArc(sketch, "E23.29.0", {"start": v(8.65, -6.79) * mm, "mid": v(8.64, -6.82) * mm, "end": v(8.65, -6.85) * mm});
            skArc(sketch, "E23.29.1", {"start": v(9.16, -7.7) * mm, "mid": v(8.93, -7.27) * mm, "end": v(8.65, -6.85) * mm});
            skArc(sketch, "E23.29.2", {"start": v(9.15, -7.76) * mm, "mid": v(9.17, -7.73) * mm, "end": v(9.16, -7.7) * mm});
            skArc(sketch, "E23.29.3", {"start": v(9.15, -7.76) * mm, "mid": v(9.04, -7.89) * mm, "end": v(8.93, -8.01) * mm});
            skArc(sketch, "E23.29.4", {"start": v(8.88, -8.03) * mm, "mid": v(8.9, -8.03) * mm, "end": v(8.93, -8.01) * mm});
            skArc(sketch, "E23.29.5", {"start": v(8.88, -8.03) * mm, "mid": v(8.41, -7.85) * mm, "end": v(7.96, -7.64) * mm});
            skArc(sketch, "E23.29.6", {"start": v(7.96, -7.64) * mm, "mid": v(7.93, -7.63) * mm, "end": v(7.9, -7.65) * mm});
            skArc(sketch, "E23.30.0", {"start": v(9.5, -5.55) * mm, "mid": v(9.5, -5.58) * mm, "end": v(9.5, -5.6) * mm});
            skArc(sketch, "E23.30.1", {"start": v(10.13, -6.38) * mm, "mid": v(9.83, -5.98) * mm, "end": v(9.5, -5.6) * mm});
            skArc(sketch, "E23.30.2", {"start": v(10.13, -6.44) * mm, "mid": v(10.13, -6.41) * mm, "end": v(10.13, -6.38) * mm});
            skArc(sketch, "E23.30.3", {"start": v(10.13, -6.44) * mm, "mid": v(10.03, -6.58) * mm, "end": v(9.94, -6.72) * mm});
            skArc(sketch, "E23.30.4", {"start": v(9.9, -6.74) * mm, "mid": v(9.92, -6.74) * mm, "end": v(9.94, -6.72) * mm});
            skArc(sketch, "E23.30.5", {"start": v(9.9, -6.74) * mm, "mid": v(9.4, -6.63) * mm, "end": v(8.93, -6.48) * mm});
            skArc(sketch, "E23.30.6", {"start": v(8.93, -6.48) * mm, "mid": v(8.9, -6.48) * mm, "end": v(8.87, -6.5) * mm});
            skArc(sketch, "E23.31.0", {"start": v(10.17, -4.2) * mm, "mid": v(10.16, -4.23) * mm, "end": v(10.18, -4.26) * mm});
            skArc(sketch, "E23.31.1", {"start": v(10.9, -4.95) * mm, "mid": v(10.56, -4.59) * mm, "end": v(10.18, -4.26) * mm});
            skArc(sketch, "E23.31.2", {"start": v(10.9, -5) * mm, "mid": v(10.91, -4.97) * mm, "end": v(10.9, -4.95) * mm});
            skArc(sketch, "E23.31.3", {"start": v(10.9, -5) * mm, "mid": v(10.84, -5.15) * mm, "end": v(10.76, -5.3) * mm});
            skArc(sketch, "E23.31.4", {"start": v(10.72, -5.33) * mm, "mid": v(10.74, -5.33) * mm, "end": v(10.76, -5.3) * mm});
            skArc(sketch, "E23.31.5", {"start": v(10.72, -5.33) * mm, "mid": v(10.22, -5.3) * mm, "end": v(9.73, -5.2) * mm});
            skArc(sketch, "E23.31.6", {"start": v(9.73, -5.2) * mm, "mid": v(9.7, -5.21) * mm, "end": v(9.68, -5.23) * mm});
            skArc(sketch, "E23.32.0", {"start": v(10.64, -2.78) * mm, "mid": v(10.65, -2.81) * mm, "end": v(10.67, -2.84) * mm});
            skArc(sketch, "E23.32.1", {"start": v(11.47, -3.42) * mm, "mid": v(11.08, -3.1) * mm, "end": v(10.67, -2.84) * mm});
            skArc(sketch, "E23.32.2", {"start": v(11.49, -3.47) * mm, "mid": v(11.49, -3.44) * mm, "end": v(11.47, -3.42) * mm});
            skArc(sketch, "E23.32.3", {"start": v(11.49, -3.47) * mm, "mid": v(11.44, -3.63) * mm, "end": v(11.39, -3.8) * mm});
            skArc(sketch, "E23.32.4", {"start": v(11.34, -3.82) * mm, "mid": v(11.37, -3.81) * mm, "end": v(11.39, -3.8) * mm});
            skArc(sketch, "E23.32.5", {"start": v(11.34, -3.82) * mm, "mid": v(10.85, -3.85) * mm, "end": v(10.35, -3.83) * mm});
            skArc(sketch, "E23.32.6", {"start": v(10.35, -3.83) * mm, "mid": v(10.32, -3.84) * mm, "end": v(10.3, -3.87) * mm});
            skArc(sketch, "E23.33.0", {"start": v(10.92, -1.3) * mm, "mid": v(10.93, -1.34) * mm, "end": v(10.95, -1.36) * mm});
            skArc(sketch, "E23.33.1", {"start": v(11.83, -1.82) * mm, "mid": v(11.4, -1.57) * mm, "end": v(10.95, -1.36) * mm});
            skArc(sketch, "E23.33.2", {"start": v(11.85, -1.87) * mm, "mid": v(11.85, -1.84) * mm, "end": v(11.83, -1.82) * mm});
            skArc(sketch, "E23.33.3", {"start": v(11.85, -1.87) * mm, "mid": v(11.83, -2.04) * mm, "end": v(11.8, -2.2) * mm});
            skArc(sketch, "E23.33.4", {"start": v(11.76, -2.24) * mm, "mid": v(11.78, -2.23) * mm, "end": v(11.8, -2.2) * mm});
            skArc(sketch, "E23.33.5", {"start": v(11.76, -2.24) * mm, "mid": v(11.27, -2.34) * mm, "end": v(10.77, -2.39) * mm});
            skArc(sketch, "E23.33.6", {"start": v(10.77, -2.39) * mm, "mid": v(10.75, -2.4) * mm, "end": v(10.73, -2.43) * mm});
            skArc(sketch, "E23.34.0", {"start": v(11, 0.2) * mm, "mid": v(11, 0.16) * mm, "end": v(11.04, 0.15) * mm});
            skArc(sketch, "E23.34.1", {"start": v(11.97, -0.2) * mm, "mid": v(11.5, 0) * mm, "end": v(11.04, 0.15) * mm});
            skArc(sketch, "E23.34.2", {"start": v(12, -0.24) * mm, "mid": v(12, -0.21) * mm, "end": v(11.97, -0.2) * mm});
            skArc(sketch, "E23.34.3", {"start": v(12, -0.24) * mm, "mid": v(12, -0.4) * mm, "end": v(11.99, -0.58) * mm});
            skArc(sketch, "E23.34.4", {"start": v(11.95, -0.62) * mm, "mid": v(11.98, -0.6) * mm, "end": v(11.99, -0.58) * mm});
            skArc(sketch, "E23.34.5", {"start": v(11.95, -0.62) * mm, "mid": v(11.48, -0.78) * mm, "end": v(11, -0.9) * mm});
            skArc(sketch, "E23.34.6", {"start": v(11, -0.9) * mm, "mid": v(10.97, -0.92) * mm, "end": v(10.96, -0.94) * mm});
            skArc(sketch, "E23.35.0", {"start": v(10.87, 1.7) * mm, "mid": v(10.88, 1.66) * mm, "end": v(10.91, 1.65) * mm});
            skArc(sketch, "E23.35.1", {"start": v(11.88, 1.44) * mm, "mid": v(11.4, 1.56) * mm, "end": v(10.91, 1.65) * mm});
            skArc(sketch, "E23.35.2", {"start": v(11.92, 1.4) * mm, "mid": v(11.9, 1.42) * mm, "end": v(11.88, 1.44) * mm});
            skArc(sketch, "E23.35.3", {"start": v(11.92, 1.4) * mm, "mid": v(11.94, 1.23) * mm, "end": v(11.95, 1.06) * mm});
            skArc(sketch, "E23.35.4", {"start": v(11.93, 1.01) * mm, "mid": v(11.95, 1.03) * mm, "end": v(11.95, 1.06) * mm});
            skArc(sketch, "E23.35.5", {"start": v(11.93, 1.01) * mm, "mid": v(11.48, 0.79) * mm, "end": v(11.02, 0.6) * mm});
            skArc(sketch, "E23.35.6", {"start": v(11.02, 0.6) * mm, "mid": v(11, 0.59) * mm, "end": v(10.99, 0.56) * mm});
            skArc(sketch, "E23.36.0", {"start": v(10.54, 3.15) * mm, "mid": v(10.56, 3.13) * mm, "end": v(10.59, 3.12) * mm});
            skArc(sketch, "E23.36.1", {"start": v(11.58, 3.04) * mm, "mid": v(11.08, 3.1) * mm, "end": v(10.59, 3.12) * mm});
            skArc(sketch, "E23.36.2", {"start": v(11.62, 3) * mm, "mid": v(11.6, 3.03) * mm, "end": v(11.58, 3.04) * mm});
            skArc(sketch, "E23.36.3", {"start": v(11.62, 3) * mm, "mid": v(11.66, 2.84) * mm, "end": v(11.7, 2.68) * mm});
            skArc(sketch, "E23.36.4", {"start": v(11.68, 2.63) * mm, "mid": v(11.7, 2.65) * mm, "end": v(11.7, 2.68) * mm});
            skArc(sketch, "E23.36.5", {"start": v(11.68, 2.63) * mm, "mid": v(11.27, 2.35) * mm, "end": v(10.83, 2.1) * mm});
            skArc(sketch, "E23.36.6", {"start": v(10.83, 2.1) * mm, "mid": v(10.81, 2.08) * mm, "end": v(10.8, 2.05) * mm});
            skArc(sketch, "E23.37.0", {"start": v(10.01, 4.56) * mm, "mid": v(10.03, 4.54) * mm, "end": v(10.06, 4.53) * mm});
            skArc(sketch, "E23.37.1", {"start": v(11.06, 4.6) * mm, "mid": v(10.56, 4.58) * mm, "end": v(10.06, 4.53) * mm});
            skArc(sketch, "E23.37.2", {"start": v(11.1, 4.56) * mm, "mid": v(11.08, 4.58) * mm, "end": v(11.06, 4.6) * mm});
            skArc(sketch, "E23.37.3", {"start": v(11.1, 4.56) * mm, "mid": v(11.16, 4.4) * mm, "end": v(11.22, 4.24) * mm});
            skArc(sketch, "E23.37.4", {"start": v(11.21, 4.2) * mm, "mid": v(11.23, 4.22) * mm, "end": v(11.22, 4.24) * mm});
            skArc(sketch, "E23.37.5", {"start": v(11.21, 4.2) * mm, "mid": v(10.84, 3.86) * mm, "end": v(10.45, 3.56) * mm});
            skArc(sketch, "E23.37.6", {"start": v(10.45, 3.56) * mm, "mid": v(10.43, 3.53) * mm, "end": v(10.43, 3.5) * mm});
            skArc(sketch, "E23.38.0", {"start": v(9.3, 5.88) * mm, "mid": v(9.32, 5.86) * mm, "end": v(9.35, 5.86) * mm});
            skArc(sketch, "E23.38.1", {"start": v(10.33, 6.05) * mm, "mid": v(9.84, 5.98) * mm, "end": v(9.35, 5.86) * mm});
            skArc(sketch, "E23.38.2", {"start": v(10.38, 6.03) * mm, "mid": v(10.36, 6.05) * mm, "end": v(10.33, 6.05) * mm});
            skArc(sketch, "E23.38.3", {"start": v(10.38, 6.03) * mm, "mid": v(10.46, 5.88) * mm, "end": v(10.54, 5.73) * mm});
            skArc(sketch, "E23.38.4", {"start": v(10.54, 5.68) * mm, "mid": v(10.55, 5.7) * mm, "end": v(10.54, 5.73) * mm});
            skArc(sketch, "E23.38.5", {"start": v(10.54, 5.68) * mm, "mid": v(10.22, 5.3) * mm, "end": v(9.87, 4.95) * mm});
            skArc(sketch, "E23.38.6", {"start": v(9.87, 4.95) * mm, "mid": v(9.85, 4.92) * mm, "end": v(9.85, 4.89) * mm});
            skArc(sketch, "E23.39.0", {"start": v(8.4, 7.1) * mm, "mid": v(8.44, 7.08) * mm, "end": v(8.47, 7.08) * mm});
            skArc(sketch, "E23.39.1", {"start": v(9.4, 7.4) * mm, "mid": v(8.93, 7.26) * mm, "end": v(8.47, 7.08) * mm});
            skArc(sketch, "E23.39.2", {"start": v(9.46, 7.38) * mm, "mid": v(9.44, 7.4) * mm, "end": v(9.4, 7.4) * mm});
            skArc(sketch, "E23.39.3", {"start": v(9.46, 7.38) * mm, "mid": v(9.56, 7.25) * mm, "end": v(9.66, 7.12) * mm});
            skArc(sketch, "E23.39.4", {"start": v(9.67, 7.06) * mm, "mid": v(9.67, 7.09) * mm, "end": v(9.66, 7.12) * mm});
            skArc(sketch, "E23.39.5", {"start": v(9.67, 7.06) * mm, "mid": v(9.4, 6.64) * mm, "end": v(9.1, 6.24) * mm});
            skArc(sketch, "E23.39.6", {"start": v(9.1, 6.24) * mm, "mid": v(9.09, 6.21) * mm, "end": v(9.1, 6.18) * mm});
            skArc(sketch, "E23.40.0", {"start": v(7.36, 8.17) * mm, "mid": v(7.4, 8.16) * mm, "end": v(7.42, 8.17) * mm});
            skArc(sketch, "E23.40.1", {"start": v(8.31, 8.61) * mm, "mid": v(7.86, 8.4) * mm, "end": v(7.42, 8.17) * mm});
            skArc(sketch, "E23.40.2", {"start": v(8.36, 8.6) * mm, "mid": v(8.34, 8.62) * mm, "end": v(8.31, 8.61) * mm});
            skArc(sketch, "E23.40.3", {"start": v(8.36, 8.6) * mm, "mid": v(8.49, 8.49) * mm, "end": v(8.6, 8.36) * mm});
            skArc(sketch, "E23.40.4", {"start": v(8.61, 8.31) * mm, "mid": v(8.62, 8.34) * mm, "end": v(8.6, 8.36) * mm});
            skArc(sketch, "E23.40.5", {"start": v(8.61, 8.31) * mm, "mid": v(8.4, 7.86) * mm, "end": v(8.17, 7.42) * mm});
            skArc(sketch, "E23.40.6", {"start": v(8.17, 7.42) * mm, "mid": v(8.16, 7.4) * mm, "end": v(8.17, 7.36) * mm});
            skArc(sketch, "E23.41.0", {"start": v(6.18, 9.1) * mm, "mid": v(6.21, 9.09) * mm, "end": v(6.24, 9.1) * mm});
            skArc(sketch, "E23.41.1", {"start": v(7.06, 9.67) * mm, "mid": v(6.64, 9.4) * mm, "end": v(6.24, 9.1) * mm});
            skArc(sketch, "E23.41.2", {"start": v(7.12, 9.66) * mm, "mid": v(7.09, 9.67) * mm, "end": v(7.06, 9.67) * mm});
            skArc(sketch, "E23.41.3", {"start": v(7.12, 9.66) * mm, "mid": v(7.25, 9.56) * mm, "end": v(7.38, 9.46) * mm});
            skArc(sketch, "E23.41.4", {"start": v(7.4, 9.4) * mm, "mid": v(7.4, 9.44) * mm, "end": v(7.38, 9.46) * mm});
            skArc(sketch, "E23.41.5", {"start": v(7.4, 9.4) * mm, "mid": v(7.26, 8.93) * mm, "end": v(7.08, 8.47) * mm});
            skArc(sketch, "E23.41.6", {"start": v(7.08, 8.47) * mm, "mid": v(7.08, 8.44) * mm, "end": v(7.1, 8.4) * mm});
            skArc(sketch, "E23.42.0", {"start": v(4.89, 9.85) * mm, "mid": v(4.92, 9.85) * mm, "end": v(4.95, 9.87) * mm});
            skArc(sketch, "E23.42.1", {"start": v(5.68, 10.54) * mm, "mid": v(5.3, 10.22) * mm, "end": v(4.95, 9.87) * mm});
            skArc(sketch, "E23.42.2", {"start": v(5.73, 10.54) * mm, "mid": v(5.7, 10.55) * mm, "end": v(5.68, 10.54) * mm});
            skArc(sketch, "E23.42.3", {"start": v(5.73, 10.54) * mm, "mid": v(5.88, 10.46) * mm, "end": v(6.03, 10.38) * mm});
            skArc(sketch, "E23.42.4", {"start": v(6.05, 10.33) * mm, "mid": v(6.05, 10.36) * mm, "end": v(6.03, 10.38) * mm});
            skArc(sketch, "E23.42.5", {"start": v(6.05, 10.33) * mm, "mid": v(5.98, 9.84) * mm, "end": v(5.86, 9.35) * mm});
            skArc(sketch, "E23.42.6", {"start": v(5.86, 9.35) * mm, "mid": v(5.86, 9.32) * mm, "end": v(5.88, 9.3) * mm});
            skArc(sketch, "E23.43.0", {"start": v(3.5, 10.43) * mm, "mid": v(3.53, 10.43) * mm, "end": v(3.56, 10.45) * mm});
            skArc(sketch, "E23.43.1", {"start": v(4.2, 11.21) * mm, "mid": v(3.86, 10.84) * mm, "end": v(3.56, 10.45) * mm});
            skArc(sketch, "E23.43.2", {"start": v(4.24, 11.22) * mm, "mid": v(4.22, 11.23) * mm, "end": v(4.2, 11.21) * mm});
            skArc(sketch, "E23.43.3", {"start": v(4.24, 11.22) * mm, "mid": v(4.4, 11.16) * mm, "end": v(4.56, 11.1) * mm});
            skArc(sketch, "E23.43.4", {"start": v(4.6, 11.06) * mm, "mid": v(4.58, 11.08) * mm, "end": v(4.56, 11.1) * mm});
            skArc(sketch, "E23.43.5", {"start": v(4.6, 11.06) * mm, "mid": v(4.58, 10.56) * mm, "end": v(4.53, 10.06) * mm});
            skArc(sketch, "E23.43.6", {"start": v(4.53, 10.06) * mm, "mid": v(4.54, 10.03) * mm, "end": v(4.56, 10.01) * mm});
            skArc(sketch, "E23.44.0", {"start": v(2.05, 10.8) * mm, "mid": v(2.08, 10.81) * mm, "end": v(2.1, 10.83) * mm});
            skArc(sketch, "E23.44.1", {"start": v(2.63, 11.68) * mm, "mid": v(2.35, 11.27) * mm, "end": v(2.1, 10.83) * mm});
            skArc(sketch, "E23.44.2", {"start": v(2.68, 11.7) * mm, "mid": v(2.65, 11.7) * mm, "end": v(2.63, 11.68) * mm});
            skArc(sketch, "E23.44.3", {"start": v(2.68, 11.7) * mm, "mid": v(2.84, 11.66) * mm, "end": v(3, 11.62) * mm});
            skArc(sketch, "E23.44.4", {"start": v(3.04, 11.58) * mm, "mid": v(3.03, 11.6) * mm, "end": v(3, 11.62) * mm});
            skArc(sketch, "E23.44.5", {"start": v(3.04, 11.58) * mm, "mid": v(3.1, 11.08) * mm, "end": v(3.12, 10.59) * mm});
            skArc(sketch, "E23.44.6", {"start": v(3.12, 10.59) * mm, "mid": v(3.13, 10.56) * mm, "end": v(3.15, 10.54) * mm});
            skArc(sketch, "E23.45.0", {"start": v(0.56, 10.99) * mm, "mid": v(0.59, 11) * mm, "end": v(0.6, 11.02) * mm});
            skArc(sketch, "E23.45.1", {"start": v(1.01, 11.93) * mm, "mid": v(0.79, 11.48) * mm, "end": v(0.6, 11.02) * mm});
            skArc(sketch, "E23.45.2", {"start": v(1.06, 11.95) * mm, "mid": v(1.03, 11.95) * mm, "end": v(1.01, 11.93) * mm});
            skArc(sketch, "E23.45.3", {"start": v(1.06, 11.95) * mm, "mid": v(1.23, 11.94) * mm, "end": v(1.4, 11.92) * mm});
            skArc(sketch, "E23.45.4", {"start": v(1.44, 11.88) * mm, "mid": v(1.42, 11.9) * mm, "end": v(1.4, 11.92) * mm});
            skArc(sketch, "E23.45.5", {"start": v(1.44, 11.88) * mm, "mid": v(1.56, 11.4) * mm, "end": v(1.65, 10.91) * mm});
            skArc(sketch, "E23.45.6", {"start": v(1.65, 10.91) * mm, "mid": v(1.66, 10.88) * mm, "end": v(1.7, 10.87) * mm});
            skSolve(sketch);
        }
        {
            var Q0;
            Q0=qSketchRegion(id+"F4",true);
            extrude(context, id + "F5", {"entities" : qUnion([Q0]), "operationType" : NewBodyOperationType.REMOVE, "endBound" : BoundingType.THROUGH_ALL, "oppositeDirection" : true, "depth" : 25 * mm});
        }
    });
